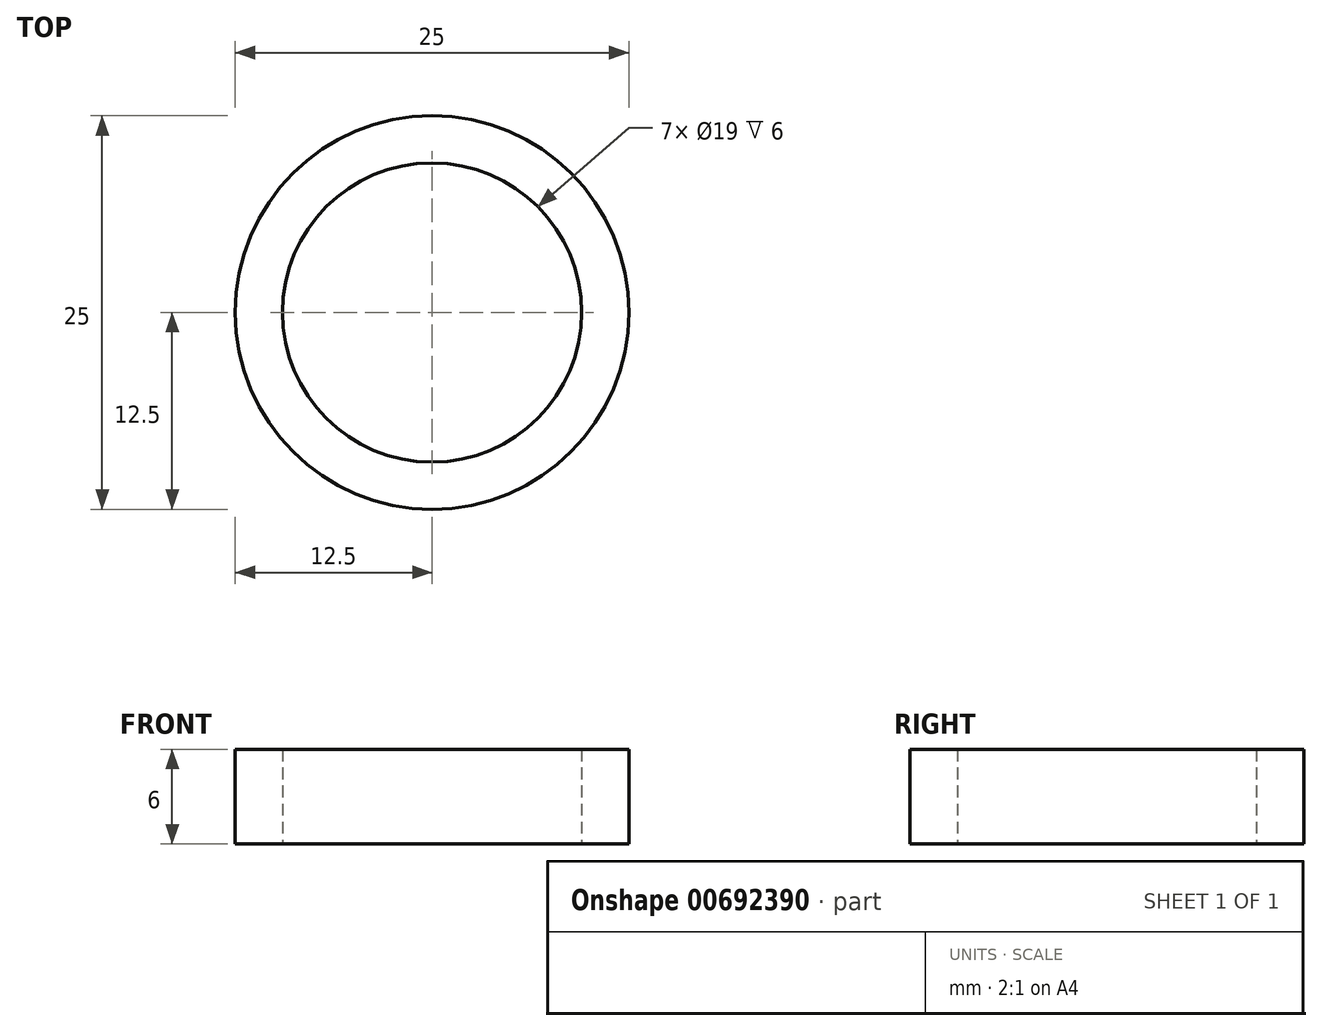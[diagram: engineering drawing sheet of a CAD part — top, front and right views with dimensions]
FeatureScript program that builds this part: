
annotation { "Feature Type Name" : "Feature", "Feature Type Description" : "" }
export const myFeature = defineFeature(function(context is Context, id is Id, definition is map)
    precondition{}
    {
        {
            var Q0;
            Q0=qCreatedBy(makeId("Top.planeOp"),FACE);
            var sketch = newSketch(context, id + "F0", { "sketchPlane" : qUnion([Q0])});
            skCircle(sketch, "E0", {"center": v(0, 0) * mm, "radius": 9.5 * mm});
            skCircle(sketch, "E1.0", {"center": v(0, 0) * mm, "radius": 12.5 * mm});
            skSolve(sketch);
        }
        {
            var Q0;
            Q0 = qSketchRegion(id + "F0", true);
            extrude(context, id + "F1", {"entities" : qUnion([Q0]), "depth" : 6 * mm, "offsetDistance" : 25 * mm});
        }
    });
